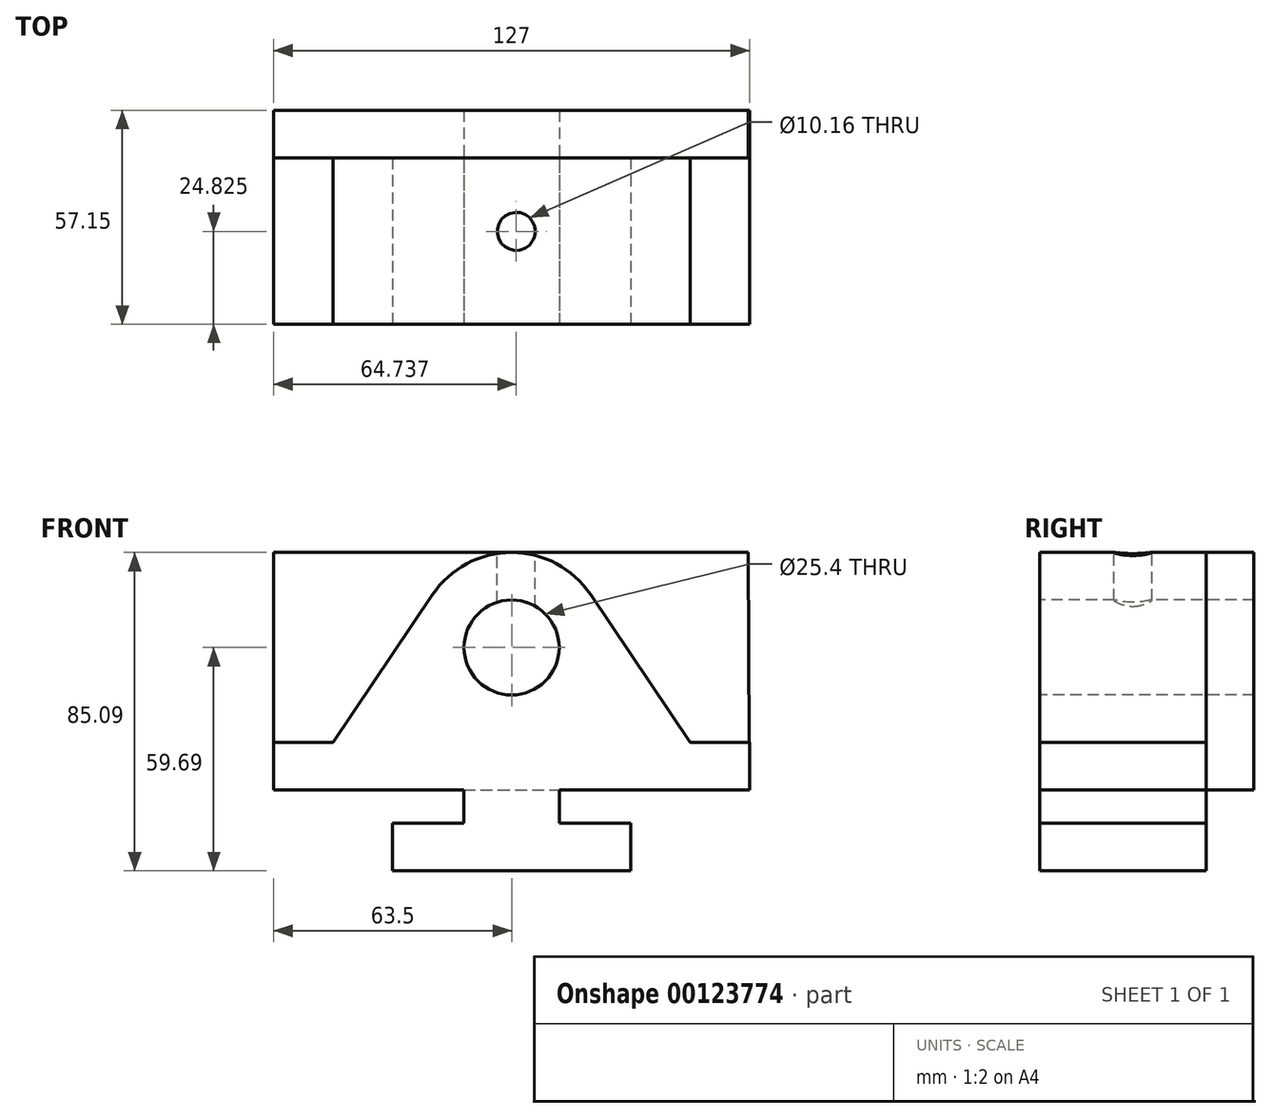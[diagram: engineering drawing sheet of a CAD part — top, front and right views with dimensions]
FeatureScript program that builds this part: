
annotation { "Feature Type Name" : "Feature", "Feature Type Description" : "" }
export const myFeature = defineFeature(function(context is Context, id is Id, definition is map)
    precondition{}
    {
        {
            var Q0;
            Q0=qCreatedBy(makeId("Front.planeOp"),FACE);
            var sketch = newSketch(context, id + "F0", { "sketchPlane" : qUnion([Q0])});
            skLineSegment(sketch, "E0", {"start": v(-50.8, 0) * mm, "end": v(-50.8, 12.7) * mm});
            skLineSegment(sketch, "E1", {"start": v(-50.8, 12.7) * mm, "end": v(-34.93, 12.7) * mm});
            skLineSegment(sketch, "E2", {"start": v(76.2, 0) * mm, "end": v(76.2, 12.7) * mm});
            skLineSegment(sketch, "E3", {"start": v(76.2, 12.7) * mm, "end": v(60.33, 12.7) * mm});
            skLineSegment(sketch, "E4", {"start": v(-50.8, 0) * mm, "end": v(0, 0) * mm});
            skLineSegment(sketch, "E5", {"start": v(0, 0) * mm, "end": v(0, -8.9) * mm});
            skLineSegment(sketch, "E6", {"start": v(0, -8.9) * mm, "end": v(-19.05, -8.9) * mm});
            skLineSegment(sketch, "E7", {"start": v(-19.05, -8.9) * mm, "end": v(-19.05, -21.6) * mm});
            skLineSegment(sketch, "E8", {"start": v(-19.05, -21.6) * mm, "end": v(44.45, -21.6) * mm});
            skLineSegment(sketch, "E9", {"start": v(44.45, -21.6) * mm, "end": v(44.45, -8.89) * mm});
            skLineSegment(sketch, "E10", {"start": v(44.45, -8.89) * mm, "end": v(25.4, -8.9) * mm});
            skLineSegment(sketch, "E11", {"start": v(25.4, -8.9) * mm, "end": v(25.4, 0) * mm});
            skLineSegment(sketch, "E12", {"start": v(25.4, 0) * mm, "end": v(76.2, 0) * mm});
            skLineSegment(sketch, "E13", {"start": v(12.7, 0) * mm, "end": v(12.7, -52.78) * mm, "construction": true});
            skLineSegment(sketch, "E14", {"start": v(-34.93, 12.7) * mm, "end": v(-8.4, 52.25) * mm});
            skLineSegment(sketch, "E15", {"start": v(60.33, 12.7) * mm, "end": v(33.8, 52.25) * mm});
            skArc(sketch, "E16", {"start": v(-8.4, 52.25) * mm, "mid": v(12.7, 63.5) * mm, "end": v(33.8, 52.25) * mm});
            skLineSegment(sketch, "E17", {"start": v(12.7, 63.5) * mm, "end": v(-27.16, 63.5) * mm, "construction": true});
            skCircle(sketch, "E18", {"center": v(12.7, 38.1) * mm, "radius": 12.7 * mm});
            skSolve(sketch);
        }
        {
            var Q0;
            Q0=makeQuery(id+"F0.imprint","IMPRINT",FACE,{"disambiguationData":[TD([[makeQuery(id+"F0.imprint","IMPRINT",EDGE,{"derivedFrom":sQuery(id+"F0.wireOp",EDGE,"E0")}),-1.0]])]});
            extrude(context, id + "F1", {"entities" : qUnion([Q0]), "oppositeDirection" : true, "depth" : 44.45 * mm});
        }
        {
            var Q0;
            Q0=makeQuery(id+"F1.opExtrude","CAP_FACE",FACE,{"disambiguationData":[OSD([sQuery(id+"F0.wireOp",EDGE,"E0"),sQuery(id+"F0.wireOp",EDGE,"E1"),sQuery(id+"F0.wireOp",EDGE,"E2"),sQuery(id+"F0.wireOp",EDGE,"E3"),sQuery(id+"F0.wireOp",EDGE,"E4"),sQuery(id+"F0.wireOp",EDGE,"E5"),sQuery(id+"F0.wireOp",EDGE,"E6"),sQuery(id+"F0.wireOp",EDGE,"E7"),sQuery(id+"F0.wireOp",EDGE,"E8"),sQuery(id+"F0.wireOp",EDGE,"E9"),sQuery(id+"F0.wireOp",EDGE,"E10"),sQuery(id+"F0.wireOp",EDGE,"E11"),sQuery(id+"F0.wireOp",EDGE,"E12"),sQuery(id+"F0.wireOp",EDGE,"E14"),sQuery(id+"F0.wireOp",EDGE,"E15"),sQuery(id+"F0.wireOp",EDGE,"E16"),sQuery(id+"F0.wireOp",EDGE,"E18")])],"isStart":false});
            var sketch = newSketch(context, id + "F2", { "sketchPlane" : qUnion([Q0])});
            skPoint(sketch, "E19.endSnap0", {"position": v(-12.7, -21.6) * mm});
            skLineSegment(sketch, "E20", {"start": v(50.8, 0) * mm, "end": v(50.8, 63.5) * mm});
            skPoint(sketch, "E20.endSnap0", {"position": v(50.8, 6.35) * mm});
            skPoint(sketch, "E20.endSnap1", {"position": v(-12.7, 63.5) * mm});
            skLineSegment(sketch, "E21", {"start": v(50.8, 63.5) * mm, "end": v(-75.85, 63.5) * mm});
            skLineSegment(sketch, "E22", {"start": v(-75.85, 63.5) * mm, "end": v(-76.2, 0) * mm});
            skLineSegment(sketch, "E23", {"start": v(-76.2, 0) * mm, "end": v(50.8, 0) * mm});
            skSolve(sketch);
        }
        {
            var Q0;
            {var subQ1=makeQuery(id+"F1.opExtrude","CAP_EDGE",EDGE,{"disambiguationData":[OSD([sQuery(id+"F0.wireOp",EDGE,"E1")])],"isStart":false});Q0=makeQuery(id+"F2.imprint","IMPRINT",FACE,{"disambiguationData":[TD([[makeQuery(id+"F2.imprint","IMPRINT",EDGE,{"derivedFrom":subQ1}),-1.0]])]});}
            var Q1;
            {var subQ0=makeQuery(id+"F1.opExtrude","CAP_EDGE",EDGE,{"disambiguationData":[OSD([sQuery(id+"F0.wireOp",EDGE,"E15")])],"isStart":false});Q1=makeQuery(id+"F2.imprint","IMPRINT",FACE,{"disambiguationData":[TD([[makeQuery(id+"F2.imprint","IMPRINT",EDGE,{"derivedFrom":subQ0}),1.0]])]});}
            var Q2;
            {var subQ7=makeQuery(id+"F1.opExtrude","CAP_EDGE",EDGE,{"disambiguationData":[OSD([sQuery(id+"F0.wireOp",EDGE,"E1")])],"isStart":false});Q2=makeQuery(id+"F2.imprint","IMPRINT",FACE,{"disambiguationData":[TD([[makeQuery(id+"F2.imprint","IMPRINT",EDGE,{"derivedFrom":subQ7}),1.0]])]});}
            extrude(context, id + "F3", {"entities" : qUnion([Q0, Q1, Q2]), "operationType" : NewBodyOperationType.ADD, "depth" : 12.7 * mm});
        }
        {
            var Q0;
            Q0=qCreatedBy(makeId("Top.planeOp"),FACE);
            cPlane(context, id + "F4", {"entities" : qUnion([Q0]), "cplaneType" : CPlaneType.OFFSET, "offset" : 76.2 * mm, "width" : 152.4 * mm, "height" : 152.4 * mm});
        }
        {
            var Q0;
            Q0=qCreatedBy(id+"F4.planeOp",FACE);
            var sketch = newSketch(context, id + "F5", { "sketchPlane" : qUnion([Q0])});
            skCircle(sketch, "E24", {"center": v(13.94, 24.82) * mm, "radius": 5.08 * mm});
            skSolve(sketch);
        }
        {
            var Q0;
            Q0=makeQuery(id+"F5.imprint","IMPRINT",FACE,{"disambiguationData":[TD([[makeQuery(id+"F5.imprint","IMPRINT",EDGE,{"derivedFrom":sQuery(id+"F5.wireOp",EDGE,"E24")}),1.0]])]});
            var Q1;
            Q1=sQuery(id+"F5.wireOp",EDGE,"E24");
            extrude(context, id + "F6", {"entities" : qUnion([Q0]), "operationType" : NewBodyOperationType.REMOVE, "surfaceEntities" : qUnion([Q1]), "oppositeDirection" : true, "depth" : 31.75 * mm});
        }
    });
